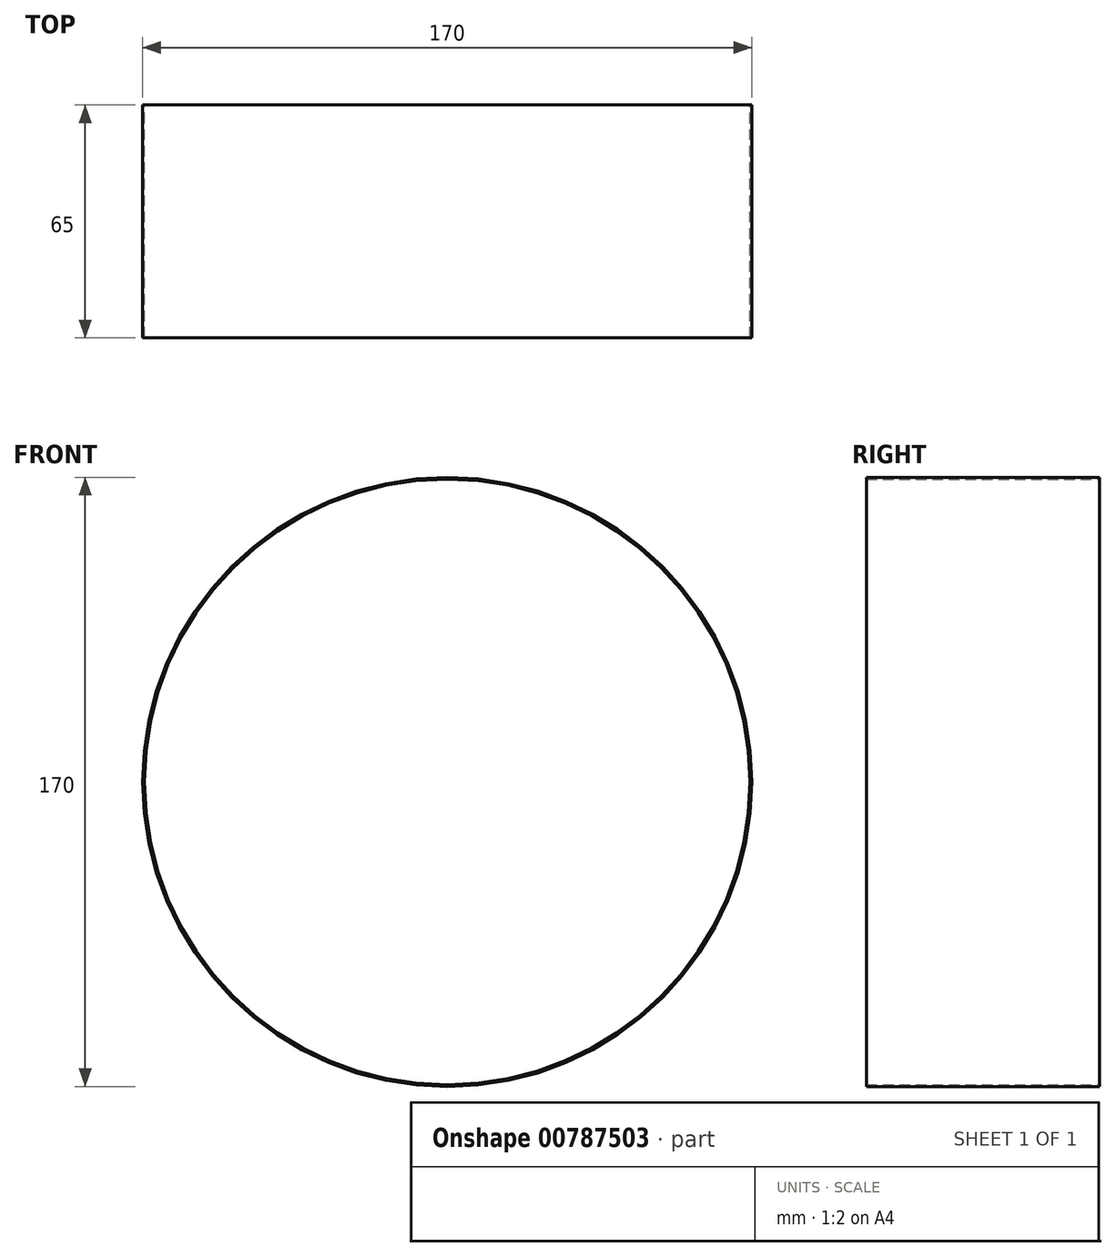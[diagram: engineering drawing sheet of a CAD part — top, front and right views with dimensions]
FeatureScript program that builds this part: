
annotation { "Feature Type Name" : "Feature", "Feature Type Description" : "" }
export const myFeature = defineFeature(function(context is Context, id is Id, definition is map)
    precondition{}
    {
        {
            var Q0;
            Q0=qCreatedBy(makeId("Front.planeOp"),FACE);
            var sketch = newSketch(context, id + "F0", { "sketchPlane" : qUnion([Q0])});
            skCircle(sketch, "E0", {"center": v(0, 0) * mm, "radius": 85 * mm});
            skCircle(sketch, "E1.0", {"center": v(0, 0) * mm, "radius": 84.5 * mm});
            skSolve(sketch);
        }
        {
            var Q0;
            Q0=makeQuery(id+"F0.imprint","IMPRINT",FACE,{"disambiguationData":[TD([[makeQuery(id+"F0.imprint","IMPRINT",EDGE,{"derivedFrom":sQuery(id+"F0.wireOp",EDGE,"E0")}),1.0]])]});
            extrude(context, id + "F1", {"entities" : qUnion([Q0]), "depth" : 65 * mm, "offsetDistance" : 25.4 * mm});
        }
    });
